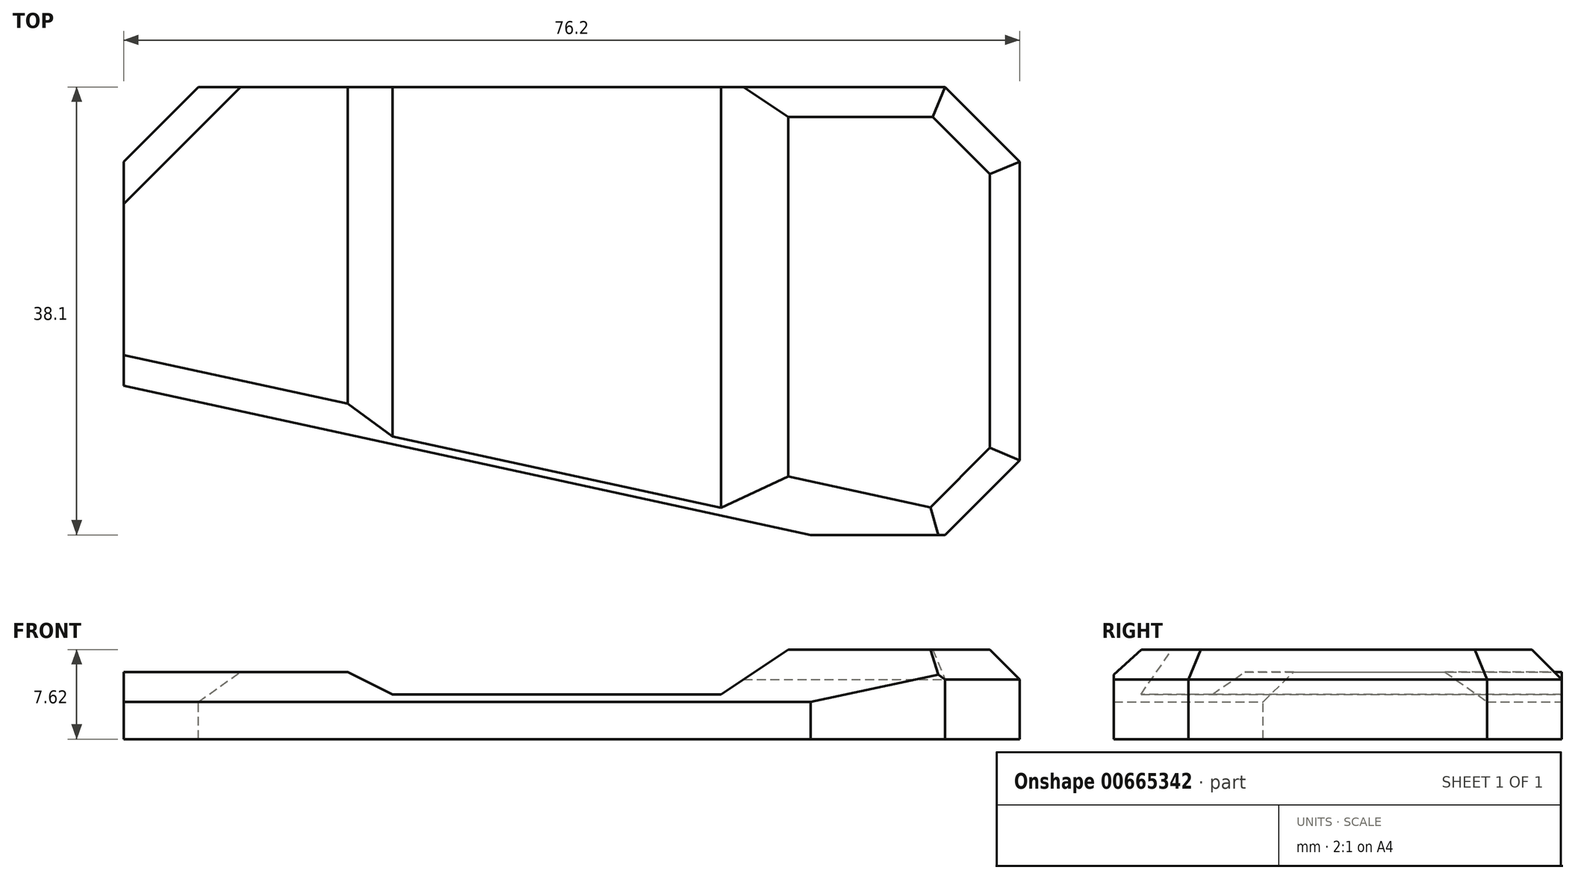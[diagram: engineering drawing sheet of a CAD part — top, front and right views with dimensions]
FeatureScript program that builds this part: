
annotation { "Feature Type Name" : "Feature", "Feature Type Description" : "" }
export const myFeature = defineFeature(function(context is Context, id is Id, definition is map)
    precondition{}
    {
        {
            var Q0;
            Q0=qCreatedBy(makeId("Top.planeOp"),FACE);
            var sketch = newSketch(context, id + "F0", { "sketchPlane" : qUnion([Q0])});
            skLineSegment(sketch, "E0.bottom", {"start": v(38.1, -19.05) * mm, "end": v(-38.1, -19.05) * mm});
            skLineSegment(sketch, "E0.top", {"start": v(38.1, 19.05) * mm, "end": v(-38.1, 19.05) * mm});
            skLineSegment(sketch, "E0.left", {"start": v(38.1, -19.05) * mm, "end": v(38.1, 19.05) * mm});
            skLineSegment(sketch, "E0.right", {"start": v(-38.1, -19.05) * mm, "end": v(-38.1, 19.05) * mm});
            skPoint(sketch, "E0.middle", {"position": v(0, 0) * mm});
            skSolve(sketch);
        }
        {
            var Q0;
            Q0=makeQuery(id+"F0.imprint","IMPRINT",FACE,{"disambiguationData":[TD([[makeQuery(id+"F0.imprint","IMPRINT",EDGE,{"derivedFrom":sQuery(id+"F0.wireOp",EDGE,"E0.bottom")}),-1.0]])]});
            extrude(context, id + "F1", {"entities" : qUnion([Q0]), "depth" : 7.62 * mm, "offsetDistance" : 25.4 * mm});
        }
        {
            var Q0;
            Q0=makeQuery(id+"F1.opExtrude","CAP_FACE",FACE,{"disambiguationData":[OSD([sQuery(id+"F0.wireOp",EDGE,"E0.bottom"),sQuery(id+"F0.wireOp",EDGE,"E0.top"),sQuery(id+"F0.wireOp",EDGE,"E0.left"),sQuery(id+"F0.wireOp",EDGE,"E0.right")])],"isStart":false});
            var sketch = newSketch(context, id + "F2", { "sketchPlane" : qUnion([Q0])});
            skLineSegment(sketch, "E1.bottom", {"start": v(20.32, -19.05) * mm, "end": v(-20.32, -19.05) * mm});
            skLineSegment(sketch, "E1.top", {"start": v(20.32, 19.05) * mm, "end": v(-20.32, 19.05) * mm});
            skLineSegment(sketch, "E1.left", {"start": v(20.32, -19.05) * mm, "end": v(20.32, 19.05) * mm});
            skLineSegment(sketch, "E1.right", {"start": v(-20.32, -19.05) * mm, "end": v(-20.32, 19.05) * mm});
            skPoint(sketch, "E1.middle", {"position": v(0, 0) * mm});
            skLineSegment(sketch, "E2.left", {"start": v(-20.32, 19.05) * mm, "end": v(-20.32, -19.05) * mm});
            skSolve(sketch);
        }
        {
            var Q0;
            {var subQ0=sQuery(id+"F2.wireOp",EDGE,"E1.left");Q0=makeQuery(id+"F2.imprint","IMPRINT",FACE,{"disambiguationData":[TD([[makeQuery(id+"F2.imprint","IMPRINT",EDGE,{"derivedFrom":subQ0}),-1.0]])]});}
            var sketch = newSketch(context, id + "F3", { "sketchPlane" : qUnion([Q0])});
            skLineSegment(sketch, "E3.0", {"start": v(-38.1, -19.05) * mm, "end": v(-38.1, 19.05) * mm});
            skLineSegment(sketch, "E4.0", {"start": v(20.32, -19.05) * mm, "end": v(-20.32, -19.05) * mm});
            skLineSegment(sketch, "E5.0", {"start": v(20.32, -19.05) * mm, "end": v(-38.1, -19.05) * mm});
            skPoint(sketch, "E6.orphan", {"position": v(38.1, -19.05) * mm});
            skLineSegment(sketch, "E7", {"start": v(-38.1, -6.35) * mm, "end": v(20.32, -19.05) * mm});
            skSolve(sketch);
        }
        {
            var Q0;
            {var subQ3=sQuery(id+"F3.wireOp",EDGE,"cd232530-1e49-4a57-8ab3-45a062eee770");Q0=makeQuery(id+"F3.imprint","IMPRINT",FACE,{"disambiguationData":[TD([[makeQuery(id+"F3.imprint","IMPRINT",EDGE,{"derivedFrom":subQ3}),-1.0]])]});}
            var Q1;
            {var subQ3=sQuery(id+"F3.wireOp",EDGE,"E7");Q1=makeQuery(id+"F3.imprint","IMPRINT",FACE,{"disambiguationData":[TD([[makeQuery(id+"F3.imprint","IMPRINT",EDGE,{"derivedFrom":subQ3}),-1.0]])]});}
            extrude(context, id + "F4", {"entities" : qUnion([Q0, Q1]), "operationType" : NewBodyOperationType.REMOVE, "endBound" : BoundingType.THROUGH_ALL, "oppositeDirection" : true, "depth" : 25.4 * mm, "offsetDistance" : 25.4 * mm});
        }
        {
            var Q0;
            Q0=makeQuery(id+"F1.opExtrude","SWEPT_FACE",FACE,{"disambiguationData":[OSD([sQuery(id+"F0.wireOp",EDGE,"E0.top")])]});
            var sketch = newSketch(context, id + "F5", { "sketchPlane" : qUnion([Q0])});
            skPoint(sketch, "E8.0", {"position": v(-20.32, 7.62) * mm});
            skPoint(sketch, "E9.0", {"position": v(20.32, 7.62) * mm});
            skLineSegment(sketch, "E10", {"start": v(-20.32, 7.62) * mm, "end": v(-20.32, 3.81) * mm});
            skLineSegment(sketch, "E11", {"start": v(20.32, 5.72) * mm, "end": v(20.32, 3.81) * mm});
            skLineSegment(sketch, "E12", {"start": v(-20.32, 3.81) * mm, "end": v(20.32, 3.81) * mm});
            skLineSegment(sketch, "E13", {"start": v(20.32, 5.72) * mm, "end": v(38.1, 5.72) * mm});
            skSolve(sketch);
        }
        {
            var Q0;
            {var subQ1=sQuery(id+"F5.wireOp",EDGE,"E10");Q0=makeQuery(id+"F5.imprint","IMPRINT",FACE,{"disambiguationData":[TD([[makeQuery(id+"F5.imprint","IMPRINT",EDGE,{"derivedFrom":subQ1}),1.0]])]});}
            extrude(context, id + "F6", {"entities" : qUnion([Q0]), "operationType" : NewBodyOperationType.REMOVE, "endBound" : BoundingType.THROUGH_ALL, "oppositeDirection" : true, "depth" : 25.4 * mm, "offsetDistance" : 25.4 * mm});
        }
        {
            var Q0;
            Q0=makeQuery(id+"F6.boolean.opBoolean","COPY",EDGE,{"derivedFrom":makeQuery(id+"F6.opExtrude","SWEPT_EDGE",EDGE,{"disambiguationData":[OSD([sQuery(id+"F5.wireOp",EDGE,"E10"),sQuery(id+"F5.wireOp",EDGE,"E12")])]})});
            chamfer(context, id + "F7", {"entities" : qUnion([Q0]), "chamferType" : ChamferType.TWO_OFFSETS, "width1" : 7.62 * mm, "oppositeDirection" : false, "width2" : 5.08 * mm, "tangentPropagation" : true});
        }
        {
            var Q0;
            Q0=makeQuery(id+"F6.boolean.opBoolean","COPY",EDGE,{"derivedFrom":makeQuery(id+"F6.opExtrude","SWEPT_EDGE",EDGE,{"disambiguationData":[OSD([sQuery(id+"F5.wireOp",EDGE,"E11"),sQuery(id+"F5.wireOp",EDGE,"E12")])]})});
            chamfer(context, id + "F8", {"entities" : qUnion([Q0]), "chamferType" : ChamferType.TWO_OFFSETS, "width1" : 2.54 * mm, "oppositeDirection" : false, "width2" : 5.08 * mm, "tangentPropagation" : true});
        }
        {
            var Q0;
            Q0=makeQuery(id+"F4.boolean.opBoolean","COPY",EDGE,{"derivedFrom":makeQuery(id+"F4.opExtrude","SWEPT_EDGE",EDGE,{"disambiguationData":[OSD([sQuery(id+"F3.wireOp",EDGE,"E3.0"),sQuery(id+"F3.wireOp",EDGE,"E7")])]})});
            var Q1;
            Q1=makeQuery(id+"F1.opExtrude","SWEPT_EDGE",EDGE,{"disambiguationData":[OSD([sQuery(id+"F0.wireOp",EDGE,"E0.bottom"),sQuery(id+"F0.wireOp",EDGE,"E0.left")])]});
            var Q2;
            Q2=makeQuery(id+"F1.opExtrude","SWEPT_EDGE",EDGE,{"disambiguationData":[OSD([sQuery(id+"F0.wireOp",EDGE,"E0.top"),sQuery(id+"F0.wireOp",EDGE,"E0.left")])]});
            var Q3;
            Q3=makeQuery(id+"F1.opExtrude","SWEPT_EDGE",EDGE,{"disambiguationData":[OSD([sQuery(id+"F0.wireOp",EDGE,"E0.top"),sQuery(id+"F0.wireOp",EDGE,"E0.right")])]});
            chamfer(context, id + "F9", {"entities" : qUnion([Q0, Q1, Q2, Q3]), "width" : 6.35 * mm, "tangentPropagation" : true});
        }
        {
            var Q0;
            Q0=makeQuery(id+"F6.boolean.opBoolean","INTERSECT",EDGE,{"derivedFrom":[makeQuery(id+"F4.boolean.opBoolean","COPY",FACE,{"derivedFrom":makeQuery(id+"F4.opExtrude","SWEPT_FACE",FACE,{"disambiguationData":[OSD([sQuery(id+"F3.wireOp",EDGE,"E7")])]})}),makeQuery(id+"F6.opExtrude","SWEPT_FACE",FACE,{"disambiguationData":[OSD([sQuery(id+"F5.wireOp",EDGE,"E13")])]})]});
            var Q1;
            Q1=makeQuery(id+"F1.opExtrude","CAP_EDGE",EDGE,{"disambiguationData":[OSD([sQuery(id+"F0.wireOp",EDGE,"E0.left")])],"isStart":false});
            var Q2;
            {var subQ0=sQuery(id+"F0.wireOp",EDGE,"E0.left");var subQ1=sQuery(id+"F0.wireOp",EDGE,"E0.bottom");Q2=makeQuery(id+"F9.opChamfer","BLEND_EDGE",EDGE,{"blendedFrom":[makeQuery(id+"F1.opExtrude","SWEPT_EDGE",EDGE,{"disambiguationData":[OSD([subQ1,subQ0])]}),makeQuery(id+"F1.opExtrude","CAP_FACE",FACE,{"disambiguationData":[OSD([subQ1,sQuery(id+"F0.wireOp",EDGE,"E0.top"),subQ0,sQuery(id+"F0.wireOp",EDGE,"E0.right")])],"isStart":false})],"blendedInto":[makeQuery(id+"F1.opExtrude","CAP_FACE",FACE,{"disambiguationData":[OSD([subQ1,sQuery(id+"F0.wireOp",EDGE,"E0.top"),subQ0,sQuery(id+"F0.wireOp",EDGE,"E0.right")])],"isStart":false})]});}
            var Q3;
            {var subQ0=sQuery(id+"F0.wireOp",EDGE,"E0.left");var subQ1=sQuery(id+"F0.wireOp",EDGE,"E0.top");Q3=makeQuery(id+"F9.opChamfer","BLEND_EDGE",EDGE,{"blendedFrom":[makeQuery(id+"F1.opExtrude","SWEPT_EDGE",EDGE,{"disambiguationData":[OSD([subQ1,subQ0])]}),makeQuery(id+"F1.opExtrude","CAP_FACE",FACE,{"disambiguationData":[OSD([sQuery(id+"F0.wireOp",EDGE,"E0.bottom"),subQ1,subQ0,sQuery(id+"F0.wireOp",EDGE,"E0.right")])],"isStart":false})],"blendedInto":[makeQuery(id+"F1.opExtrude","CAP_FACE",FACE,{"disambiguationData":[OSD([sQuery(id+"F0.wireOp",EDGE,"E0.bottom"),subQ1,subQ0,sQuery(id+"F0.wireOp",EDGE,"E0.right")])],"isStart":false})]});}
            var Q4;
            Q4=makeQuery(id+"F1.opExtrude","CAP_EDGE",EDGE,{"disambiguationData":[OSD([sQuery(id+"F0.wireOp",EDGE,"E0.top")])],"isStart":false});
            var Q5;
            Q5=makeQuery(id+"F9.opChamfer","BLEND_EDGE",EDGE,{"blendedFrom":[makeQuery(id+"F4.boolean.opBoolean","COPY",EDGE,{"derivedFrom":makeQuery(id+"F4.opExtrude","SWEPT_EDGE",EDGE,{"disambiguationData":[OSD([sQuery(id+"F3.wireOp",EDGE,"E3.0"),sQuery(id+"F3.wireOp",EDGE,"E7")])]})}),makeQuery(id+"F6.boolean.opBoolean","COPY",FACE,{"derivedFrom":makeQuery(id+"F6.opExtrude","SWEPT_FACE",FACE,{"disambiguationData":[OSD([sQuery(id+"F5.wireOp",EDGE,"E13")])]})})],"blendedInto":[makeQuery(id+"F6.boolean.opBoolean","COPY",FACE,{"derivedFrom":makeQuery(id+"F6.opExtrude","SWEPT_FACE",FACE,{"disambiguationData":[OSD([sQuery(id+"F5.wireOp",EDGE,"E13")])]})})]});
            var Q6;
            Q6=makeQuery(id+"F6.boolean.opBoolean","COPY",EDGE,{"derivedFrom":makeQuery(id+"F6.opExtrude","SWEPT_EDGE",EDGE,{"disambiguationData":[OSD([sQuery(id+"F0.wireOp",EDGE,"E0.top"),sQuery(id+"F0.wireOp",EDGE,"E0.right"),sQuery(id+"F5.wireOp",EDGE,"E13")])]})});
            var Q7;
            Q7=makeQuery(id+"F9.opChamfer","BLEND_EDGE",EDGE,{"blendedFrom":[makeQuery(id+"F1.opExtrude","SWEPT_EDGE",EDGE,{"disambiguationData":[OSD([sQuery(id+"F0.wireOp",EDGE,"E0.top"),sQuery(id+"F0.wireOp",EDGE,"E0.right")])]}),makeQuery(id+"F6.boolean.opBoolean","COPY",FACE,{"derivedFrom":makeQuery(id+"F6.opExtrude","SWEPT_FACE",FACE,{"disambiguationData":[OSD([sQuery(id+"F5.wireOp",EDGE,"E13")])]})})],"blendedInto":[makeQuery(id+"F6.boolean.opBoolean","COPY",FACE,{"derivedFrom":makeQuery(id+"F6.opExtrude","SWEPT_FACE",FACE,{"disambiguationData":[OSD([sQuery(id+"F5.wireOp",EDGE,"E13")])]})})]});
            var Q8;
            Q8=makeQuery(id+"F6.boolean.opBoolean","COPY",EDGE,{"derivedFrom":makeQuery(id+"F6.opExtrude","CAP_EDGE",EDGE,{"disambiguationData":[OSD([sQuery(id+"F5.wireOp",EDGE,"E13")])],"isStart":true})});
            chamfer(context, id + "F10", {"entities" : qUnion([Q0, Q1, Q2, Q3, Q4, Q5, Q6, Q7, Q8]), "width" : 2.54 * mm, "tangentPropagation" : true});
        }
    });
